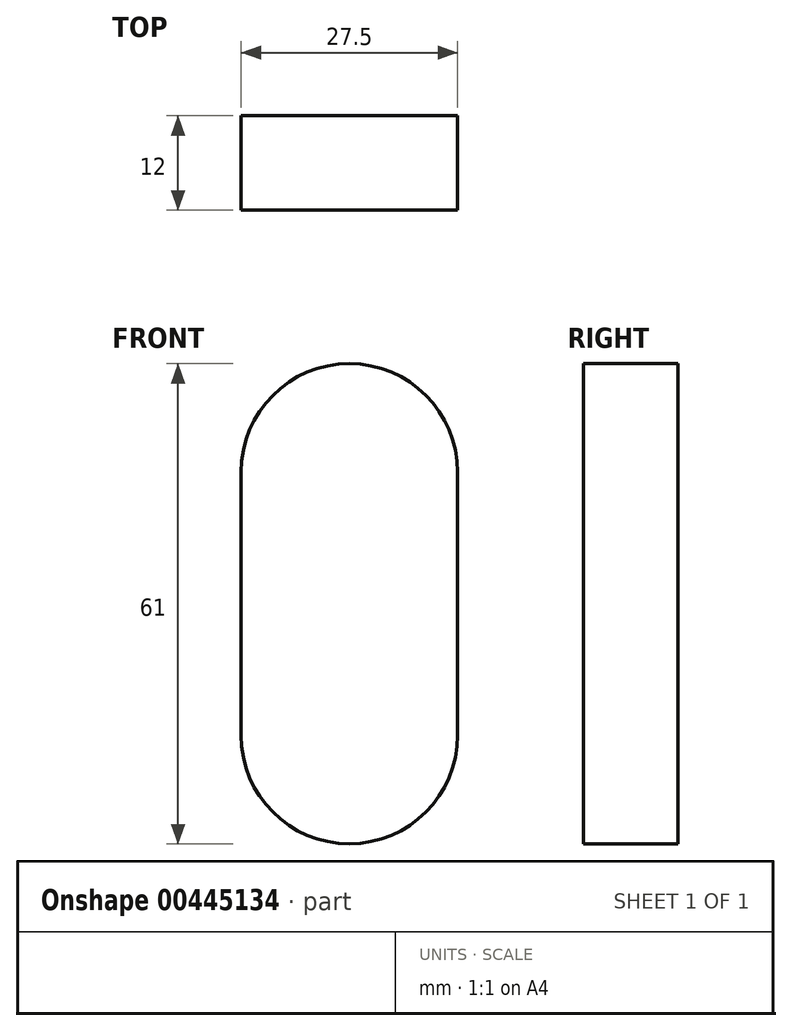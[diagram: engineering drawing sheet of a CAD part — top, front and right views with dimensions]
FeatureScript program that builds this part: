
annotation { "Feature Type Name" : "Feature", "Feature Type Description" : "" }
export const myFeature = defineFeature(function(context is Context, id is Id, definition is map)
    precondition{}
    {
        {
            var Q0;
            Q0=qCreatedBy(makeId("Front.planeOp"),FACE);
            var sketch = newSketch(context, id + "F0", { "sketchPlane" : qUnion([Q0])});
            skArc(sketch, "E0", {"start": v(-13.75, 0) * mm, "mid": v(0, -13.75) * mm, "end": v(13.75, 0) * mm});
            skArc(sketch, "E1", {"start": v(13.75, 33.5) * mm, "mid": v(0, 47.25) * mm, "end": v(-13.75, 33.5) * mm});
            skLineSegment(sketch, "E2", {"start": v(-13.75, 33.5) * mm, "end": v(-13.75, 0) * mm});
            skLineSegment(sketch, "E3", {"start": v(13.75, 33.5) * mm, "end": v(13.75, 0) * mm});
            skSolve(sketch);
        }
        {
            var Q0;
            Q0=qSketchRegion(id+"F0",true);
            extrude(context, id + "F1", {"entities" : qUnion([Q0]), "depth" : 12 * mm});
        }
    });
